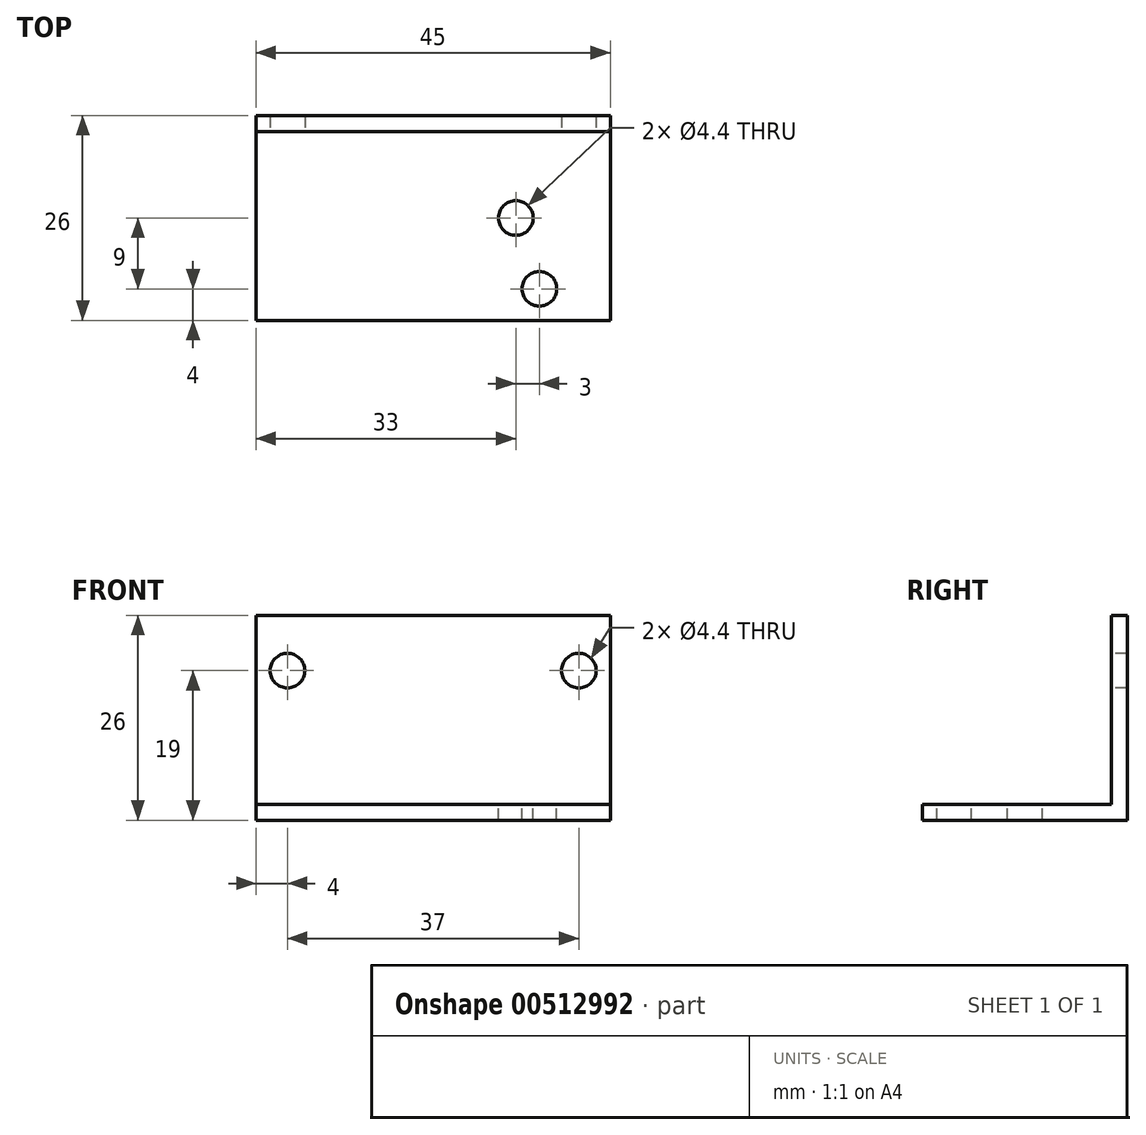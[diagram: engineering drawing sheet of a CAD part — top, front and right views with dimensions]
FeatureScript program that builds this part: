
annotation { "Feature Type Name" : "Feature", "Feature Type Description" : "" }
export const myFeature = defineFeature(function(context is Context, id is Id, definition is map)
    precondition{}
    {
        {
            var Q0;
            Q0=qCreatedBy(makeId("Top.planeOp"),FACE);
            var sketch = newSketch(context, id + "F0", { "sketchPlane" : qUnion([Q0])});
            skLineSegment(sketch, "E0.bottom", {"start": v(-33, 13) * mm, "end": v(12, 13) * mm});
            skLineSegment(sketch, "E0.top", {"start": v(-33, -13) * mm, "end": v(12, -13) * mm});
            skLineSegment(sketch, "E0.left", {"start": v(-33, 13) * mm, "end": v(-33, -13) * mm});
            skLineSegment(sketch, "E0.right", {"start": v(12, 13) * mm, "end": v(12, -13) * mm});
            skSolve(sketch);
        }
        {
            var Q0;
            Q0=qSketchRegion(id+"F0",true);
            extrude(context, id + "F1", {"entities" : qUnion([Q0]), "depth" : 26 * mm});
        }
        {
            var Q0;
            Q0=makeQuery(id+"F1.opExtrude","SWEPT_FACE",FACE,{"disambiguationData":[OSD([sQuery(id+"F0.wireOp",EDGE,"E0.right")])]});
            var sketch = newSketch(context, id + "F2", { "sketchPlane" : qUnion([Q0])});
            skLineSegment(sketch, "E1.bottom", {"start": v(-13, 26) * mm, "end": v(11, 26) * mm});
            skLineSegment(sketch, "E1.top", {"start": v(-13, 2) * mm, "end": v(11, 2) * mm});
            skLineSegment(sketch, "E1.left", {"start": v(-13, 26) * mm, "end": v(-13, 2) * mm});
            skLineSegment(sketch, "E1.right", {"start": v(11, 26) * mm, "end": v(11, 2) * mm});
            skSolve(sketch);
        }
        {
            var Q0;
            Q0=qSketchRegion(id+"F2",true);
            extrude(context, id + "F3", {"entities" : qUnion([Q0]), "operationType" : NewBodyOperationType.REMOVE, "endBound" : BoundingType.THROUGH_ALL, "oppositeDirection" : true, "depth" : 25 * mm});
        }
        {
            var Q0;
            Q0=makeQuery(id+"F3.boolean.opBoolean","COPY",FACE,{"derivedFrom":makeQuery(id+"F3.opExtrude","SWEPT_FACE",FACE,{"disambiguationData":[OSD([sQuery(id+"F2.wireOp",EDGE,"E1.top")])]})});
            var sketch = newSketch(context, id + "F4", { "sketchPlane" : qUnion([Q0])});
            skPoint(sketch, "E2", {"position": v(3, -9) * mm});
            skPoint(sketch, "E3", {"position": v(0, 0) * mm});
            skSolve(sketch);
        }
        {
            var Q0;
            Q0=sQuery(id+"F4.wireOp",VERTEX,"E3");
            var Q1;
            Q1=sQuery(id+"F4.wireOp",VERTEX,"E2");
            var Q2;
            Q2=makeQuery(id+"F1.opExtrude","SWEPT_BODY",BODY,{"disambiguationData":[OSD([sQuery(id+"F0.wireOp",EDGE,"E0.bottom"),sQuery(id+"F0.wireOp",EDGE,"E0.top"),sQuery(id+"F0.wireOp",EDGE,"E0.left"),sQuery(id+"F0.wireOp",EDGE,"E0.right")])]});
            hole(context, id + "F5", {"style" : HoleStyle.SIMPLE, "endStyle" : HoleEndStyle.THROUGH, "standardTappedOrClearance" : lookupTablePath({ "standard" : "ISO", "fit" : "Normal", "size" : "M4", "type" : "Clearance" }), "standardBlindInLast" : lookupTablePath({ "fit" : "Standard", "standard" : "ISO", "size" : "M4", "type" : "Clearance" }), "holeDiameter" : 4.4 * mm, "isTappedThrough" : true, "tappedDepth" : 12 * mm, "tapClearance" : 3, "locations" : qUnion([Q0, Q1]), "scope" : qUnion([Q2])});
        }
        {
            var Q0;
            Q0=makeQuery(id+"F3.boolean.opBoolean","COPY",FACE,{"derivedFrom":makeQuery(id+"F3.opExtrude","SWEPT_FACE",FACE,{"disambiguationData":[OSD([sQuery(id+"F2.wireOp",EDGE,"E1.right")])]})});
            var sketch = newSketch(context, id + "F6", { "sketchPlane" : qUnion([Q0])});
            skPoint(sketch, "E4", {"position": v(-29, 19) * mm});
            skPoint(sketch, "E5", {"position": v(8, 19) * mm});
            skSolve(sketch);
        }
        {
            var Q0;
            Q0=sQuery(id+"F6.wireOp",VERTEX,"E4");
            var Q1;
            Q1=sQuery(id+"F6.wireOp",VERTEX,"E5");
            var Q2;
            Q2=makeQuery(id+"F1.opExtrude","SWEPT_BODY",BODY,{"disambiguationData":[OSD([sQuery(id+"F0.wireOp",EDGE,"E0.bottom"),sQuery(id+"F0.wireOp",EDGE,"E0.top"),sQuery(id+"F0.wireOp",EDGE,"E0.left"),sQuery(id+"F0.wireOp",EDGE,"E0.right")])]});
            hole(context, id + "F7", {"style" : HoleStyle.SIMPLE, "endStyle" : HoleEndStyle.THROUGH, "standardTappedOrClearance" : lookupTablePath({ "standard" : "ISO", "fit" : "Normal", "size" : "M4", "type" : "Clearance" }), "standardBlindInLast" : lookupTablePath({ "fit" : "Standard", "standard" : "ISO", "size" : "M4", "type" : "Clearance" }), "holeDiameter" : 4.4 * mm, "isTappedThrough" : true, "tappedDepth" : 12 * mm, "tapClearance" : 3, "locations" : qUnion([Q0, Q1]), "scope" : qUnion([Q2])});
        }
    });
